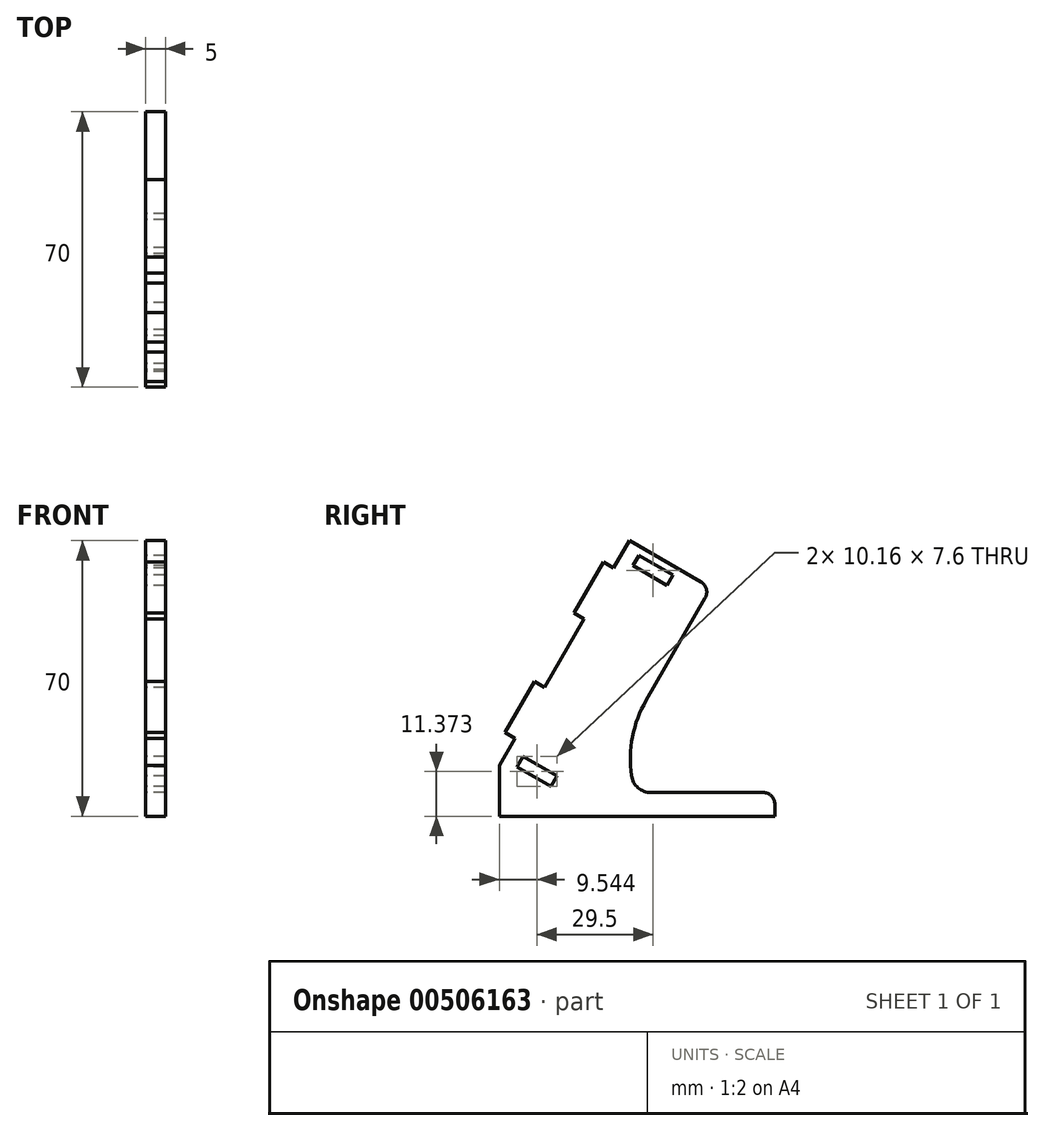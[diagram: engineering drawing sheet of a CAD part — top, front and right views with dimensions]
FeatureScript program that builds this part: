
annotation { "Feature Type Name" : "Feature", "Feature Type Description" : "" }
export const myFeature = defineFeature(function(context is Context, id is Id, definition is map)
    precondition{}
    {
        {
            var Q0;
            Q0=qCreatedBy(makeId("Right.planeOp"),FACE);
            var sketch = newSketch(context, id + "F0", { "sketchPlane" : qUnion([Q0])});
            skLineSegment(sketch, "E0", {"start": v(0, 12.84) * mm, "end": v(4, 19.77) * mm});
            skLineSegment(sketch, "E1", {"start": v(29, 63.07) * mm, "end": v(33, 70) * mm});
            skLineSegment(sketch, "E2", {"start": v(33, 70) * mm, "end": v(51.19, 59.5) * mm});
            skLineSegment(sketch, "E3", {"start": v(70, 0) * mm, "end": v(0, 0) * mm});
            skLineSegment(sketch, "E4", {"start": v(35.46, 66.27) * mm, "end": v(33.96, 63.67) * mm});
            skLineSegment(sketch, "E5", {"start": v(33.96, 63.67) * mm, "end": v(42.62, 58.67) * mm});
            skLineSegment(sketch, "E6", {"start": v(42.62, 58.67) * mm, "end": v(44.12, 61.27) * mm});
            skLineSegment(sketch, "E7", {"start": v(44.12, 61.27) * mm, "end": v(35.46, 66.27) * mm});
            skLineSegment(sketch, "E8", {"start": v(52.28, 55.4) * mm, "end": v(37.28, 29.42) * mm});
            skLineSegment(sketch, "E9", {"start": v(38.5, 6) * mm, "end": v(67, 6) * mm});
            skLineSegment(sketch, "E10", {"start": v(70, 3) * mm, "end": v(70, 0) * mm});
            skArc(sketch, "E11.filletArc", {"start": v(33.55, 10.32) * mm, "mid": v(35.22, 7.23) * mm, "end": v(38.5, 6) * mm});
            skArc(sketch, "E12.filletArc", {"start": v(37.28, 29.42) * mm, "mid": v(33.82, 20.18) * mm, "end": v(33.55, 10.32) * mm});
            skPoint(sketch, "E13.visualSharp", {"position": v(70, 6) * mm});
            skArc(sketch, "E13.filletArc", {"start": v(70, 3) * mm, "mid": v(69.12, 5.12) * mm, "end": v(67, 6) * mm});
            skPoint(sketch, "E14.visualSharp", {"position": v(53.78, 58) * mm});
            skArc(sketch, "E14.filletArc", {"start": v(52.28, 55.4) * mm, "mid": v(52.58, 57.68) * mm, "end": v(51.19, 59.5) * mm});
            skLineSegment(sketch, "E15", {"start": v(0, 0) * mm, "end": v(0, 12.84) * mm});
            skLineSegment(sketch, "E16", {"start": v(29, 63.07) * mm, "end": v(26.4, 64.57) * mm});
            skLineSegment(sketch, "E17", {"start": v(26.4, 64.57) * mm, "end": v(18.9, 51.58) * mm});
            skLineSegment(sketch, "E18", {"start": v(18.9, 51.58) * mm, "end": v(21.5, 50.08) * mm});
            skLineSegment(sketch, "E19", {"start": v(21.5, 50.08) * mm, "end": v(11.5, 32.76) * mm});
            skLineSegment(sketch, "E20", {"start": v(11.5, 32.76) * mm, "end": v(8.9, 34.26) * mm});
            skLineSegment(sketch, "E21", {"start": v(8.9, 34.26) * mm, "end": v(1.4, 21.27) * mm});
            skLineSegment(sketch, "E22", {"start": v(1.4, 21.27) * mm, "end": v(4, 19.77) * mm});
            skLineSegment(sketch, "E23", {"start": v(18.59, 40.22) * mm, "end": v(30.02, 33.62) * mm, "construction": true});
            skLineSegment(sketch, "E24.MirrorCS", {"start": v(5.96, 15.17) * mm, "end": v(14.62, 10.17) * mm});
            skLineSegment(sketch, "E25.MirrorCS", {"start": v(13.12, 7.57) * mm, "end": v(4.46, 12.57) * mm});
            skLineSegment(sketch, "E26.MirrorCS", {"start": v(14.62, 10.17) * mm, "end": v(13.12, 7.57) * mm});
            skLineSegment(sketch, "E27.MirrorCS", {"start": v(4.46, 12.57) * mm, "end": v(5.96, 15.17) * mm});
            skLineSegment(sketch, "E28", {"start": v(47.67, 57.4) * mm, "end": v(44.23, 51.45) * mm, "construction": true});
            skSolve(sketch);
        }
        {
            var Q0;
            Q0=makeQuery(id+"F0.imprint","IMPRINT",FACE,{"disambiguationData":[TD([[makeQuery(id+"F0.imprint","IMPRINT",EDGE,{"derivedFrom":sQuery(id+"F0.wireOp",EDGE,"E0")}),-1.0]])]});
            extrude(context, id + "F1", {"entities" : qUnion([Q0]), "depth" : 5 * mm});
        }
    });
